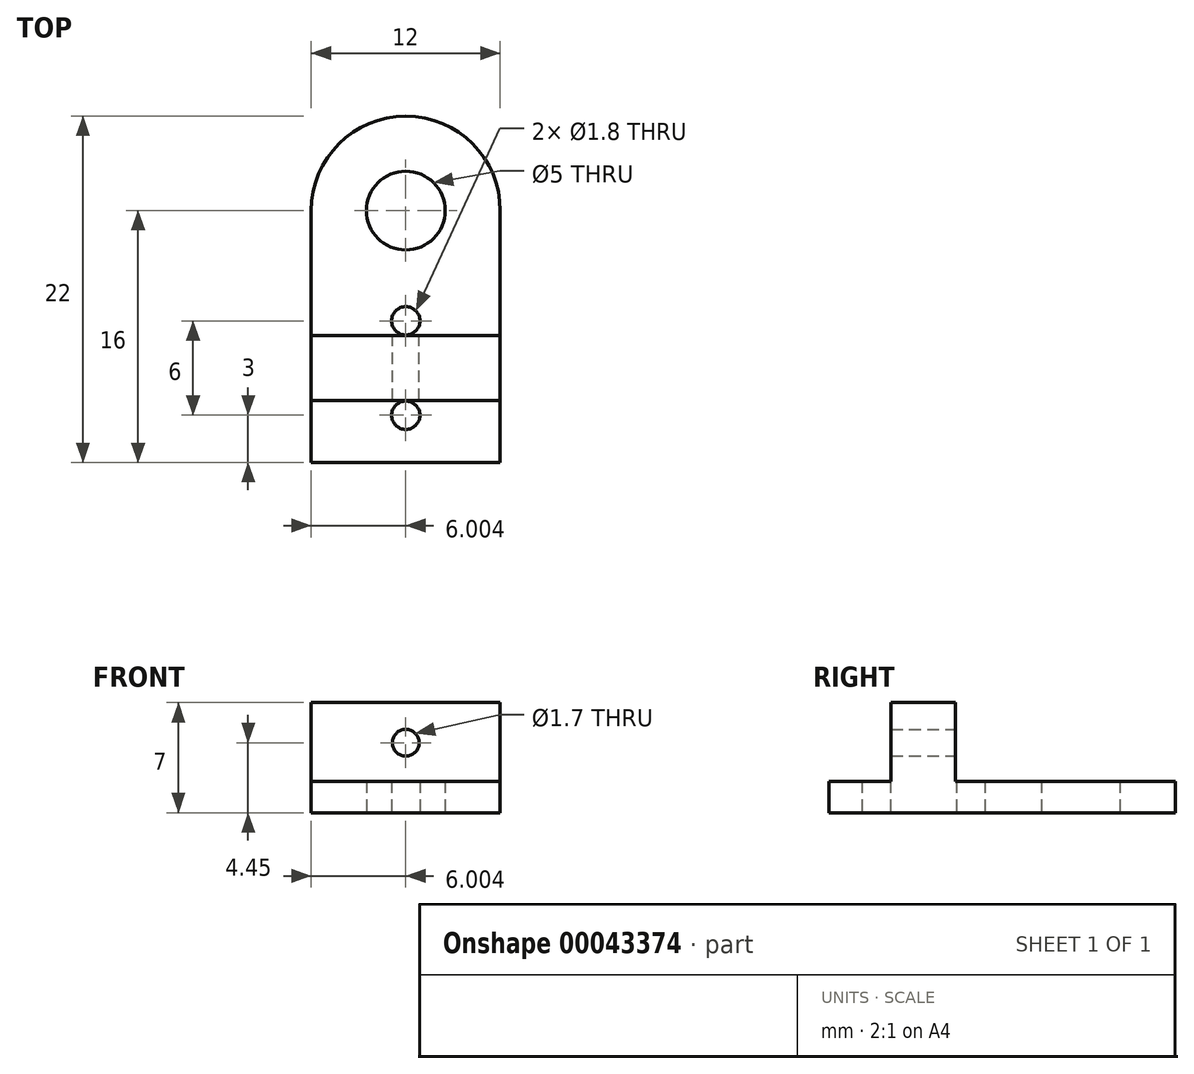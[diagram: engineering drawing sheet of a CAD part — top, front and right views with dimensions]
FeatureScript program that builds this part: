
annotation { "Feature Type Name" : "Feature", "Feature Type Description" : "" }
export const myFeature = defineFeature(function(context is Context, id is Id, definition is map)
    precondition{}
    {
        {
            var Q0;
            Q0=qCreatedBy(makeId("Top.planeOp"),FACE);
            var sketch = newSketch(context, id + "F0", { "sketchPlane" : qUnion([Q0])});
            skLineSegment(sketch, "E0", {"start": v(-0.37, 16) * mm, "end": v(-0.37, -6) * mm, "construction": true});
            skLineSegment(sketch, "E1.right", {"start": v(5.63, 16) * mm, "end": v(5.63, -6) * mm, "construction": true});
            skCircle(sketch, "E2", {"center": v(-0.37, -3) * mm, "radius": 0.9 * mm});
            skCircle(sketch, "E3", {"center": v(-0.37, 3) * mm, "radius": 0.9 * mm});
            skLineSegment(sketch, "E1.left", {"start": v(-6.37, 16) * mm, "end": v(-6.37, -6) * mm, "construction": true});
            skLineSegment(sketch, "E1.bottom", {"start": v(-6.37, 16) * mm, "end": v(5.63, 16) * mm, "construction": true});
            skCircle(sketch, "E4", {"center": v(-0.37, 10) * mm, "radius": 4 * mm});
            skLineSegment(sketch, "E1.top", {"start": v(-6.37, -6) * mm, "end": v(5.63, -6) * mm, "construction": true});
            skLineSegment(sketch, "E5", {"start": v(-6.37, 10) * mm, "end": v(5.63, 10) * mm, "construction": true});
            skLineSegment(sketch, "E6.bottom", {"start": v(-6.37, 16) * mm, "end": v(5.63, 16) * mm});
            skLineSegment(sketch, "E6.top", {"start": v(-6.37, -6) * mm, "end": v(5.63, -6) * mm});
            skLineSegment(sketch, "E6.left", {"start": v(-6.37, 16) * mm, "end": v(-6.37, -6) * mm});
            skLineSegment(sketch, "E6.right", {"start": v(5.63, 16) * mm, "end": v(5.63, -6) * mm});
            skLineSegment(sketch, "E7.bottom", {"start": v(-6.37, 2.05) * mm, "end": v(5.63, 2.05) * mm});
            skLineSegment(sketch, "E7.top", {"start": v(-6.37, -2.05) * mm, "end": v(5.63, -2.05) * mm});
            skLineSegment(sketch, "E7.left", {"start": v(-6.37, 2.05) * mm, "end": v(-6.37, -2.05) * mm});
            skLineSegment(sketch, "E7.right", {"start": v(5.63, 2.05) * mm, "end": v(5.63, -2.05) * mm});
            skPoint(sketch, "E8", {"position": v(-0.37, 0) * mm});
            skLineSegment(sketch, "E9", {"start": v(-6.37, 0) * mm, "end": v(5.63, 0) * mm, "construction": true});
            skCircle(sketch, "E10", {"center": v(-0.37, 10) * mm, "radius": 2.5 * mm});
            skSolve(sketch);
        }
        {
            var Q0;
            Q0=makeQuery(id+"F0.imprint","IMPRINT",FACE,{"disambiguationData":[TD([[makeQuery(id+"F0.imprint","IMPRINT",EDGE,{"derivedFrom":sQuery(id+"F0.wireOp",EDGE,"E7.bottom")}),-1.0]])]});
            extrude(context, id + "F1", {"entities" : qUnion([Q0]), "depth" : 7 * mm});
        }
        {
            var Q0;
            Q0=makeQuery(id+"F0.imprint","IMPRINT",FACE,{"disambiguationData":[TD([[makeQuery(id+"F0.imprint","IMPRINT",EDGE,{"derivedFrom":sQuery(id+"F0.wireOp",EDGE,"E3")}),-1.0]])]});
            var Q1;
            Q1=makeQuery(id+"F0.imprint","IMPRINT",FACE,{"disambiguationData":[TD([[makeQuery(id+"F0.imprint","IMPRINT",EDGE,{"derivedFrom":sQuery(id+"F0.wireOp",EDGE,"E2")}),-1.0]])]});
            var Q2;
            Q2=makeQuery(id+"F0.imprint","IMPRINT",FACE,{"disambiguationData":[TD([[makeQuery(id+"F0.imprint","IMPRINT",EDGE,{"derivedFrom":sQuery(id+"F0.wireOp",EDGE,"E4")}),1.0]])]});
            extrude(context, id + "F2", {"entities" : qUnion([Q0, Q1, Q2]), "operationType" : NewBodyOperationType.ADD, "depth" : 2 * mm});
        }
        {
            var Q0;
            {var subQ0=sQuery(id+"F0.wireOp",EDGE,"E7.top");var subQ1=sQuery(id+"F0.wireOp",EDGE,"E2");var subQ3=makeQuery(id+"F0.imprint","INTERSECT",VERTEX,{"disambiguationData":[OD(0.0)],"derivedFrom":[subQ1,subQ0]});Q0=makeQuery(id+"F0.imprint","IMPRINT",FACE,{"disambiguationData":[TD([[makeQuery(id+"F0.imprint","IMPRINT",EDGE,{"disambiguationData":[TD([[subQ3,1.0]])],"derivedFrom":subQ1}),1.0]])]});}
            var Q1;
            {var subQ0=sQuery(id+"F0.wireOp",EDGE,"E7.bottom");var subQ1=sQuery(id+"F0.wireOp",EDGE,"E3");var subQ3=makeQuery(id+"F0.imprint","INTERSECT",VERTEX,{"disambiguationData":[OD(0.0)],"derivedFrom":[subQ1,subQ0]});Q1=makeQuery(id+"F0.imprint","IMPRINT",FACE,{"disambiguationData":[TD([[makeQuery(id+"F0.imprint","IMPRINT",EDGE,{"disambiguationData":[TD([[subQ3,-1.0]])],"derivedFrom":subQ1}),1.0]])]});}
            extrude(context, id + "F3", {"entities" : qUnion([Q0, Q1]), "operationType" : NewBodyOperationType.REMOVE, "depth" : 2 * mm});
        }
        {
            var Q0;
            Q0=makeQuery(id+"F1.opExtrude","SWEPT_FACE",FACE,{"disambiguationData":[OSD([sQuery(id+"F0.wireOp",EDGE,"E7.bottom")])]});
            var sketch = newSketch(context, id + "F4", { "sketchPlane" : qUnion([Q0])});
            skLineSegment(sketch, "E11.bottom", {"start": v(-5.63, 7) * mm, "end": v(6.37, 7) * mm, "construction": true});
            skLineSegment(sketch, "E11.top", {"start": v(-5.63, 2) * mm, "end": v(6.37, 2) * mm, "construction": true});
            skLineSegment(sketch, "E11.left", {"start": v(-5.63, 7) * mm, "end": v(-5.63, 2) * mm, "construction": true});
            skLineSegment(sketch, "E11.right", {"start": v(6.37, 7) * mm, "end": v(6.37, 2) * mm, "construction": true});
            skLineSegment(sketch, "E12", {"start": v(0.37, 7) * mm, "end": v(0.37, 2) * mm, "construction": true});
            skCircle(sketch, "E13", {"center": v(0.37, 4.45) * mm, "radius": 0.85 * mm});
            skSolve(sketch);
        }
        {
            var Q0;
            Q0=makeQuery(id+"F4.imprint","IMPRINT",FACE,{"disambiguationData":[TD([[makeQuery(id+"F4.imprint","IMPRINT",EDGE,{"derivedFrom":sQuery(id+"F4.wireOp",EDGE,"E13")}),1.0]])]});
            extrude(context, id + "F5", {"entities" : qUnion([Q0]), "operationType" : NewBodyOperationType.REMOVE, "oppositeDirection" : true, "depth" : 5 * mm});
        }
        {
            var Q0;
            Q0=makeQuery(id+"F2.opExtrude","SWEPT_EDGE",EDGE,{"disambiguationData":[OSD([sQuery(id+"F0.wireOp",EDGE,"E6.bottom"),sQuery(id+"F0.wireOp",EDGE,"E6.right")])]});
            var Q1;
            Q1=makeQuery(id+"F2.opExtrude","SWEPT_EDGE",EDGE,{"disambiguationData":[OSD([sQuery(id+"F0.wireOp",EDGE,"E6.bottom"),sQuery(id+"F0.wireOp",EDGE,"E6.left")])]});
            fillet(context, id + "F6", {"entities" : qUnion([Q0, Q1]), "radius" : 6 * mm, "tangentPropagation" : true, "allowEdgeOverflow" : false});
        }
    });
